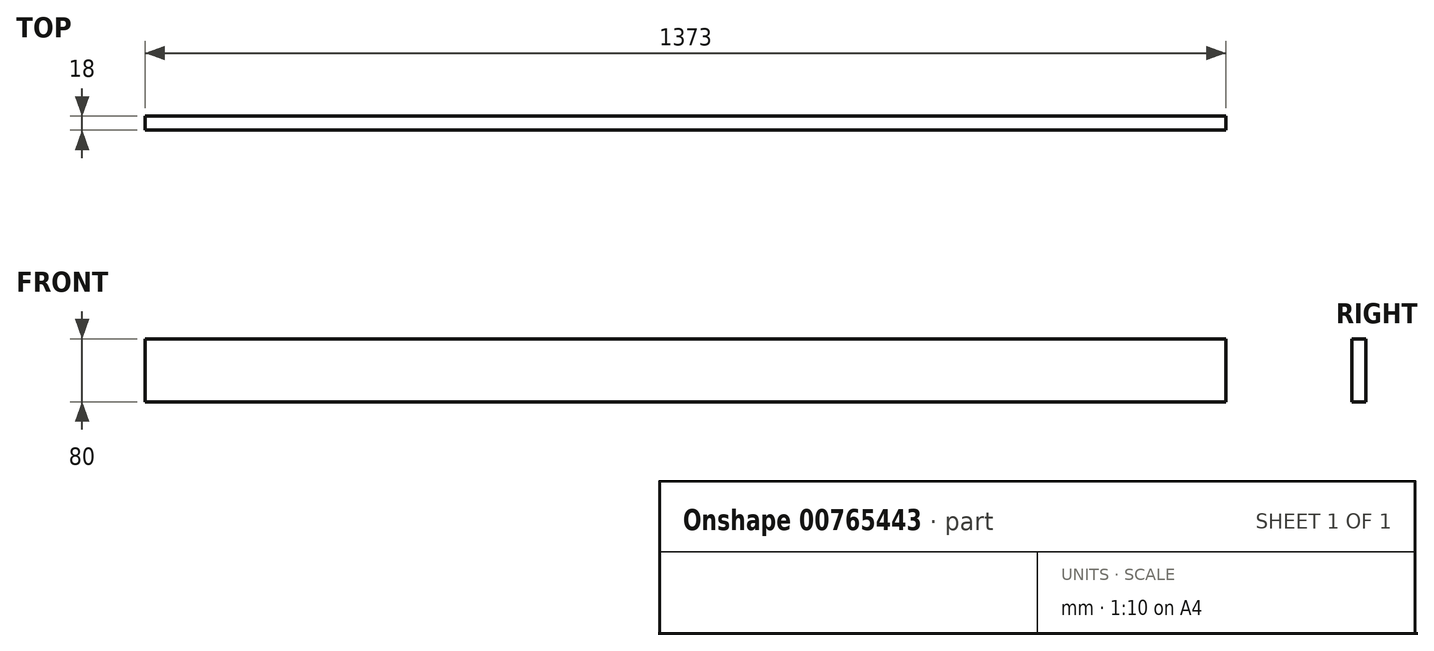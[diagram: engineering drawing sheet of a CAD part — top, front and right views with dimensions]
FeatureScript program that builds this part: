
annotation { "Feature Type Name" : "Feature", "Feature Type Description" : "" }
export const myFeature = defineFeature(function(context is Context, id is Id, definition is map)
    precondition{}
    {
        {
            var Q0;
            Q0=qCreatedBy(makeId("Front.planeOp"),FACE);
            var sketch = newSketch(context, id + "F0", { "sketchPlane" : qUnion([Q0])});
            skLineSegment(sketch, "E0.bottom", {"start": v(-686.5, -40) * mm, "end": v(686.5, -40) * mm});
            skLineSegment(sketch, "E0.top", {"start": v(-686.5, 40) * mm, "end": v(686.5, 40) * mm});
            skLineSegment(sketch, "E0.left", {"start": v(-686.5, -40) * mm, "end": v(-686.5, 40) * mm});
            skLineSegment(sketch, "E0.right", {"start": v(686.5, -40) * mm, "end": v(686.5, 40) * mm});
            skPoint(sketch, "E0.middle", {"position": v(0, 0) * mm});
            skSolve(sketch);
        }
        {
            var Q0;
            Q0 = qSketchRegion(id + "F0", true);
            extrude(context, id + "F1", {"entities" : qUnion([Q0]), "depth" : 18 * mm, "offsetDistance" : 25 * mm});
        }
    });
